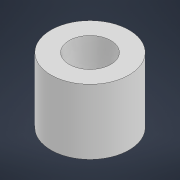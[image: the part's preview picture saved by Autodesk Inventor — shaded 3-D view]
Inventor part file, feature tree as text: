
AUTODESK INVENTOR PART (.ipt)
format: ipt  version: 2021 (Build 250183000, 183)  size: 89,600 bytes
history: native  units: mm
features: extrude x1, sketch x1
ambient origin geometry x8: Origin, YZ Plane, XZ Plane, XY Plane, X Axis, Y Axis, Z Axis, Center Point
bodies: Volumenkörper1 (feature_tree)
feature tree (2):
  extrude  "Extrusion1"  Depth=5.0mm
  sketch  "Skizze1"  dims[d0=3.2mm d1=6.0mm d2=5.0mm d3=0.0mm]
